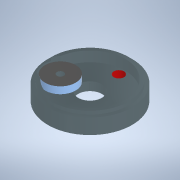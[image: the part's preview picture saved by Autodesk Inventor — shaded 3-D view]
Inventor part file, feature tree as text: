
AUTODESK INVENTOR PART (.ipt)
format: ipt  version: 2020 (Build 240168000, 168)  size: 195,072 bytes
history: native  units: mm
features: extrude x9, sketch x9, other x1
ambient origin geometry x8: Origin, YZ Plane, XZ Plane, XY Plane, X Axis, Y Axis, Z Axis, Center Point
bodies: Body1 (feature_tree)
feature tree (19):
  other  "Bryła1"
  extrude  "Wyciągnięcie proste1"  Depth=24.7mm
  extrude  "Wyciągnięcie proste2"  Depth=2.5mm TaperAngle=0.0deg
  extrude  "Wyciągnięcie proste3"  Depth=7.0mm
  extrude  "Wyciągnięcie proste4"  Depth=2.5mm TaperAngle=0.0deg
  extrude  "Wyciągnięcie proste6"  Depth=3.0mm
  extrude  "Wyciągnięcie proste7"  Depth=3.0mm
  extrude  "Wyciągnięcie proste5"  Depth=17.0mm
  extrude  "Wyciągnięcie proste8"  Depth=8.5mm
  extrude  "Wyciągnięcie proste9"  Depth=2.5mm TaperAngle=0.0deg
  sketch  "Szkic1"
  sketch  "Szkic2"
  sketch  "Szkic3"
  sketch  "Szkic4"
  sketch  "Szkic5"
  sketch  "Szkic6"
  sketch  "Szkic7"
  sketch  "Szkic8"
  sketch  "Szkic9"
